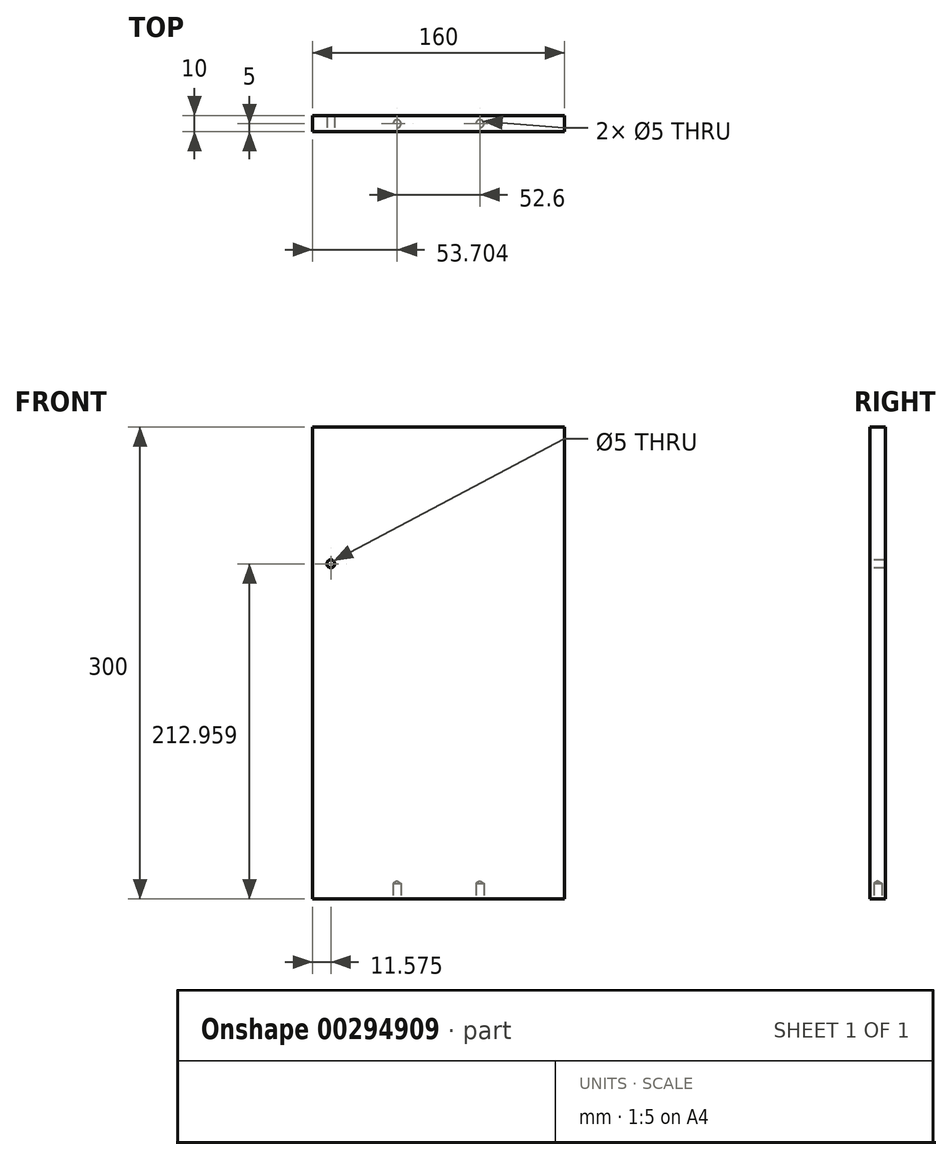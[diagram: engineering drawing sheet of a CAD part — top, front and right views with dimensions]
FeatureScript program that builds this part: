
annotation { "Feature Type Name" : "Feature", "Feature Type Description" : "" }
export const myFeature = defineFeature(function(context is Context, id is Id, definition is map)
    precondition{}
    {
        {
            var Q0;
            Q0=qCreatedBy(makeId("Front.planeOp"),FACE);
            var sketch = newSketch(context, id + "F0", { "sketchPlane" : qUnion([Q0])});
            skLineSegment(sketch, "E0.bottom", {"start": v(-54.85, 244.8) * mm, "end": v(105.15, 244.8) * mm});
            skLineSegment(sketch, "E0.top", {"start": v(-54.85, -55.2) * mm, "end": v(105.15, -55.2) * mm});
            skLineSegment(sketch, "E0.left", {"start": v(-54.85, 244.8) * mm, "end": v(-54.85, -55.2) * mm});
            skLineSegment(sketch, "E0.right", {"start": v(105.15, 244.8) * mm, "end": v(105.15, -55.2) * mm});
            skSolve(sketch);
        }
        {
            var Q0;
            Q0=makeQuery(id+"F0.imprint","IMPRINT",FACE,{"disambiguationData":[TD([[makeQuery(id+"F0.imprint","IMPRINT",EDGE,{"derivedFrom":sQuery(id+"F0.wireOp",EDGE,"E0.bottom")}),-1.0]])]});
            extrude(context, id + "F1", {"entities" : qUnion([Q0]), "depth" : 10 * mm});
        }
        {
            var Q0;
            Q0=makeQuery(id+"F1.opExtrude","SWEPT_FACE",FACE,{"disambiguationData":[OSD([sQuery(id+"F0.wireOp",EDGE,"E0.top")])]});
            var sketch = newSketch(context, id + "F2", { "sketchPlane" : qUnion([Q0])});
            skLineSegment(sketch, "E1", {"start": v(-54.85, 5) * mm, "end": v(105.15, 5) * mm, "construction": true});
            skPoint(sketch, "E2", {"position": v(-1.15, 5) * mm});
            skPoint(sketch, "E3", {"position": v(51.45, 5) * mm});
            skSolve(sketch);
        }
        {
            var Q0;
            Q0=sQuery(id+"F2.wireOp",VERTEX,"E2");
            var Q1;
            Q1=sQuery(id+"F2.wireOp",VERTEX,"E3");
            var Q2;
            Q2=makeQuery(id+"F1.opExtrude","SWEPT_BODY",BODY,{"disambiguationData":[OSD([sQuery(id+"F0.wireOp",EDGE,"E0.bottom"),sQuery(id+"F0.wireOp",EDGE,"E0.top"),sQuery(id+"F0.wireOp",EDGE,"E0.left"),sQuery(id+"F0.wireOp",EDGE,"E0.right")])]});
            hole(context, id + "F3", {"style" : HoleStyle.SIMPLE, "endStyle" : HoleEndStyle.BLIND, "holeDiameter" : 5 * mm, "holeDepth" : 10 * mm, "tappedDepth" : 12 * mm, "tapClearance" : 3, "locations" : qUnion([Q0, Q1]), "scope" : qUnion([Q2])});
        }
        {
            var Q0;
            Q0=makeQuery(id+"F1.opExtrude","CAP_FACE",FACE,{"disambiguationData":[OSD([sQuery(id+"F0.wireOp",EDGE,"E0.bottom"),sQuery(id+"F0.wireOp",EDGE,"E0.top"),sQuery(id+"F0.wireOp",EDGE,"E0.left"),sQuery(id+"F0.wireOp",EDGE,"E0.right")])],"isStart":false});
            var sketch = newSketch(context, id + "F4", { "sketchPlane" : qUnion([Q0])});
            skLineSegment(sketch, "E4", {"start": v(-54.85, 137.8) * mm, "end": v(105.15, 137.8) * mm});
            skLineSegment(sketch, "E5", {"start": v(-54.85, 137.8) * mm, "end": v(105.15, 230.16) * mm});
            skLineSegment(sketch, "E6", {"start": v(-49.42, 168.4) * mm, "end": v(-19.62, 116.77) * mm});
            skPoint(sketch, "E7", {"position": v(-43.27, 157.75) * mm});
            skSolve(sketch);
        }
        {
            var Q0;
            Q0=sQuery(id+"F4.wireOp",VERTEX,"E7");
            var Q1;
            Q1=makeQuery(id+"F1.opExtrude","SWEPT_BODY",BODY,{"disambiguationData":[OSD([sQuery(id+"F0.wireOp",EDGE,"E0.bottom"),sQuery(id+"F0.wireOp",EDGE,"E0.top"),sQuery(id+"F0.wireOp",EDGE,"E0.left"),sQuery(id+"F0.wireOp",EDGE,"E0.right")])]});
            hole(context, id + "F5", {"style" : HoleStyle.SIMPLE, "endStyle" : HoleEndStyle.THROUGH, "holeDiameter" : 5 * mm, "tappedDepth" : 12 * mm, "tapClearance" : 3, "locations" : qUnion([Q0]), "scope" : qUnion([Q1])});
        }
    });
